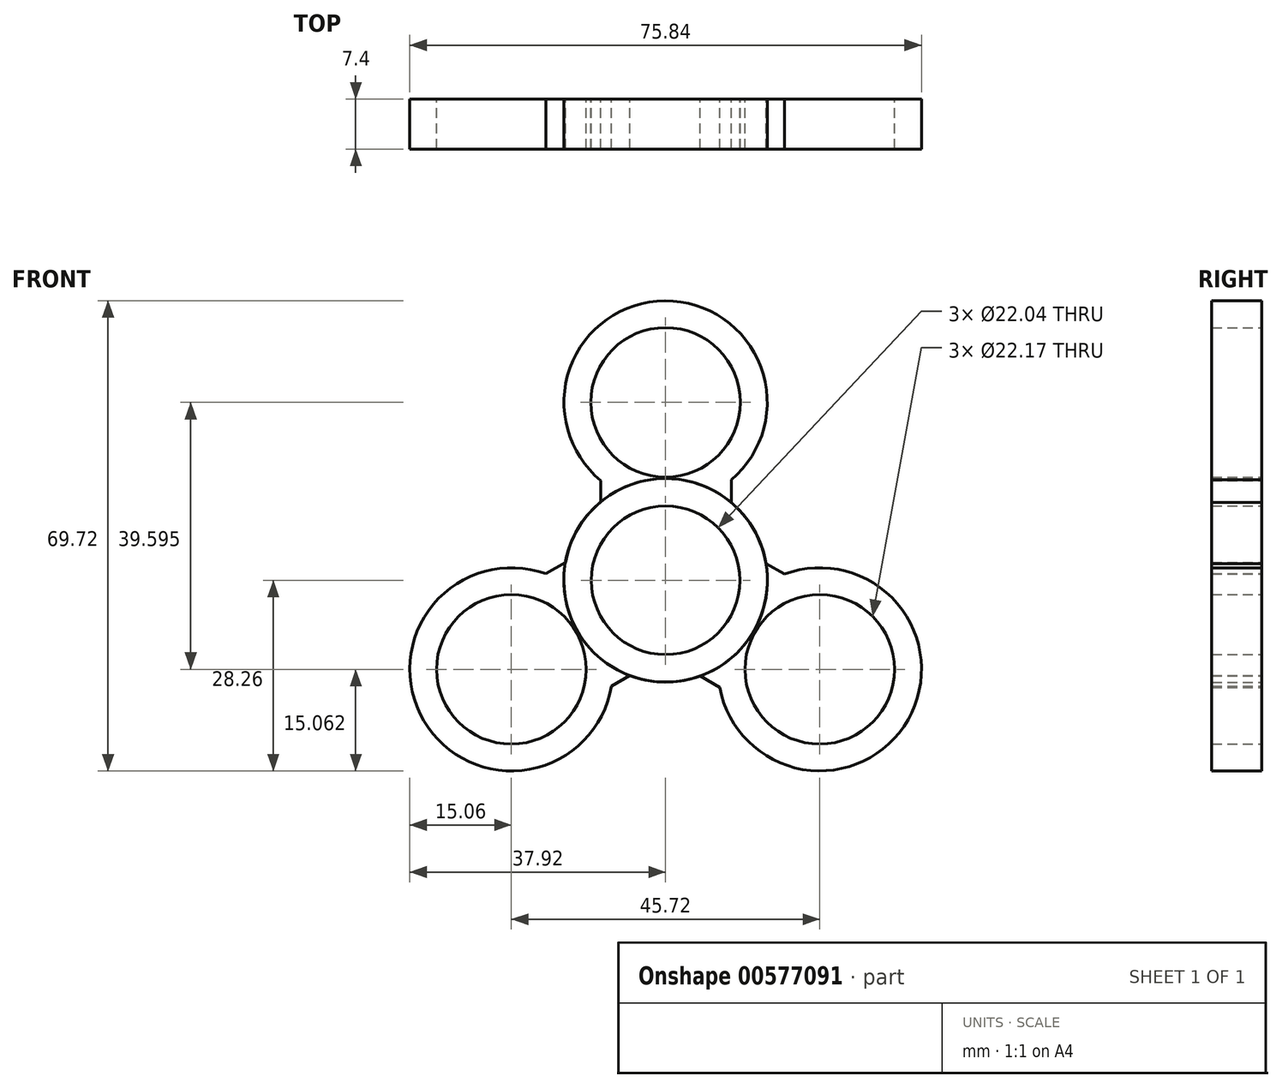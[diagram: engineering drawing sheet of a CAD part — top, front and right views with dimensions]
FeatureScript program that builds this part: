
annotation { "Feature Type Name" : "Feature", "Feature Type Description" : "" }
export const myFeature = defineFeature(function(context is Context, id is Id, definition is map)
    precondition{}
    {
        {
            var Q0;
            Q0=qCreatedBy(makeId("Front.planeOp"),FACE);
            var sketch = newSketch(context, id + "F0", { "sketchPlane" : qUnion([Q0])});
            skCircle(sketch, "E0", {"center": v(0, 0) * mm, "radius": 11.02 * mm});
            skCircle(sketch, "E1", {"center": v(0, 0) * mm, "radius": 15.1 * mm});
            skCircle(sketch, "E2", {"center": v(0, 26.4) * mm, "radius": 15.06 * mm});
            skCircle(sketch, "E3", {"center": v(0, 26.4) * mm, "radius": 11.08 * mm});
            skLineSegment(sketch, "E4", {"start": v(-9.6, 14.8) * mm, "end": v(-9.6, 11.64) * mm});
            skLineSegment(sketch, "E5", {"start": v(9.74, 14.9) * mm, "end": v(9.74, 11.53) * mm});
            skSolve(sketch);
        }
        {
            var Q0;
            Q0 = qSketchRegion(id + "F0", true);
            var Q1;
            {var subQ0=sQuery(id+"F0.wireOp",EDGE,"E2");var subQ1=sQuery(id+"F0.wireOp",EDGE,"E1");var subQ2=makeQuery(id+"F0.imprint","INTERSECT",VERTEX,{"disambiguationData":[OD(0.0)],"derivedFrom":[subQ1,subQ0]});Q1=makeQuery(id+"F0.imprint","IMPRINT",FACE,{"disambiguationData":[TD([[makeQuery(id+"F0.imprint","IMPRINT",EDGE,{"disambiguationData":[TD([[subQ2,-1.0]])],"derivedFrom":subQ1}),1.0]])]});}
            extrude(context, id + "F1", {"entities" : qUnion([Q0, Q1]), "depth" : 7.4 * mm, "offsetDistance" : 25 * mm});
        }
        {
            var Q0;
            Q0=makeQuery(id+"F1.opExtrude","SWEPT_BODY",BODY,{"disambiguationData":[OSD([sQuery(id+"F0.wireOp",EDGE,"E0"),sQuery(id+"F0.wireOp",EDGE,"E1"),sQuery(id+"F0.wireOp",EDGE,"E2"),sQuery(id+"F0.wireOp",EDGE,"E3"),sQuery(id+"F0.wireOp",EDGE,"E4"),sQuery(id+"F0.wireOp",EDGE,"E5")])]});
            var Q1;
            Q1=makeQuery(id+"F1.opExtrude","CAP_EDGE",EDGE,{"disambiguationData":[OSD([sQuery(id+"F0.wireOp",EDGE,"E0")])],"isStart":false});
            transform(context, id + "F2", {"entities" : qUnion([Q0]), "transformType" : TransformType.ROTATION, "transformAxis" : qUnion([Q1]), "angle" : 120 * degree, "makeCopy" : true});
        }
        {
            var Q0;
            Q0=makeQuery(id+"F2.opPattern","COPY",BODY,{"derivedFrom":makeQuery(id+"F1.opExtrude","SWEPT_BODY",BODY,{"disambiguationData":[OSD([sQuery(id+"F0.wireOp",EDGE,"E0"),sQuery(id+"F0.wireOp",EDGE,"E1"),sQuery(id+"F0.wireOp",EDGE,"E2"),sQuery(id+"F0.wireOp",EDGE,"E3"),sQuery(id+"F0.wireOp",EDGE,"E4"),sQuery(id+"F0.wireOp",EDGE,"E5")])]}),"instanceName":"1"});
            var Q1;
            Q1=makeQuery(id+"F1.opExtrude","CAP_EDGE",EDGE,{"disambiguationData":[OSD([sQuery(id+"F0.wireOp",EDGE,"E0")])],"isStart":false});
            transform(context, id + "F3", {"entities" : qUnion([Q0]), "transformType" : TransformType.ROTATION, "transformAxis" : qUnion([Q1]), "angle" : 120 * degree, "makeCopy" : true});
        }
    });
